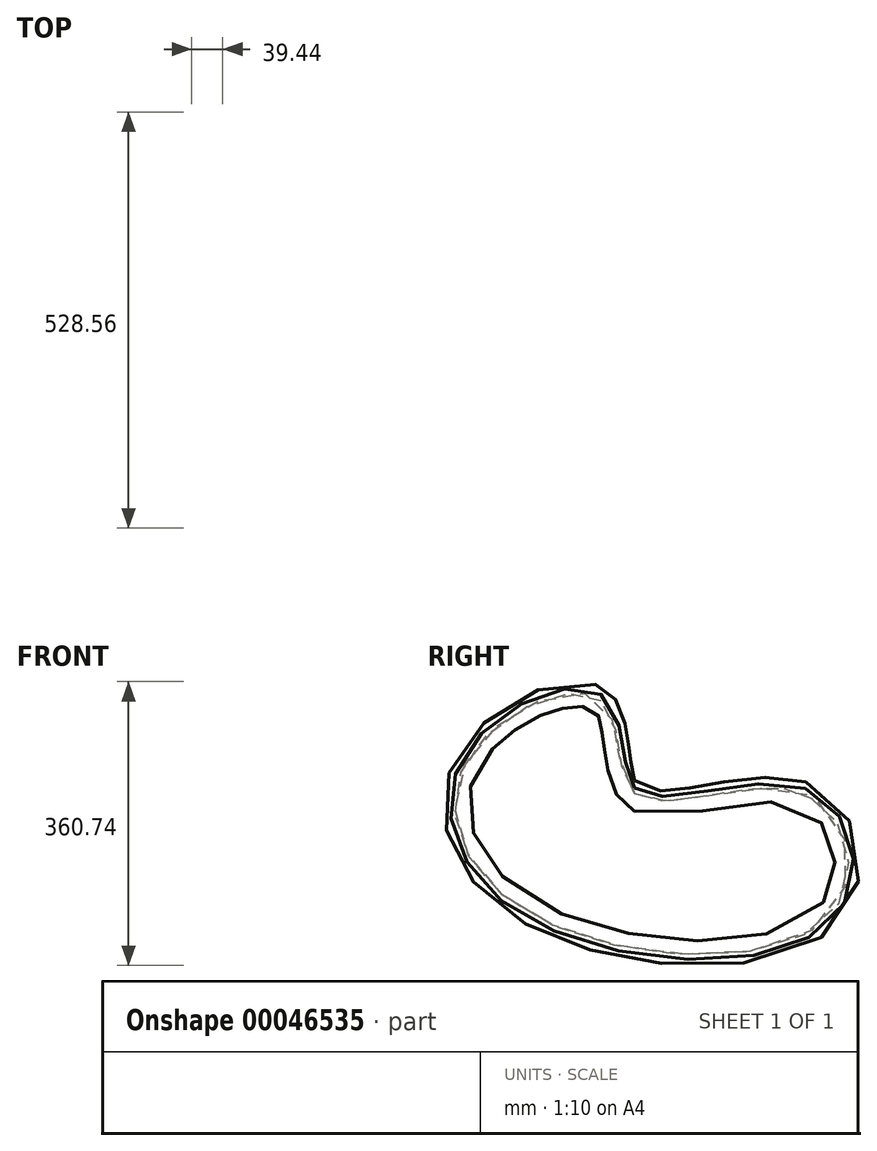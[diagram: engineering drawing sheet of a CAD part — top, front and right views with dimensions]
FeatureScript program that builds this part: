
annotation { "Feature Type Name" : "Feature", "Feature Type Description" : "" }
export const myFeature = defineFeature(function(context is Context, id is Id, definition is map)
    precondition{}
    {
        {
            var Q0;
            Q0=qCreatedBy(makeId("Front.planeOp"),FACE);
            var sketch = newSketch(context, id + "F0", { "sketchPlane" : qUnion([Q0])});
            skCircle(sketch, "E0", {"center": v(0, 0) * mm, "radius": 19.72 * mm});
            skCircle(sketch, "E1", {"center": v(-18.56, 6.66) * mm, "radius": 3.98 * mm});
            skSolve(sketch);
        }
        {
            var Q0;
            Q0=qCreatedBy(makeId("Right.planeOp"),FACE);
            var sketch = newSketch(context, id + "F1", { "sketchPlane" : qUnion([Q0])});
            skFitSpline(sketch, "E2", {"points": [v(0, 0) * mm, v(216.74, 0) * mm, v(247.02, -149.99) * mm, v(-145.22, -140.2) * mm, v(-207.64, 49.86) * mm, v(-44.13, 119.27) * mm, v(0, 0) * mm]});
            skSolve(sketch);
        }
        {
            var Q0;
            {var subQ0=sQuery(id+"F0.wireOp",EDGE,"E1");var subQ1=sQuery(id+"F0.wireOp",EDGE,"E0");var subQ3=makeQuery(id+"F0.imprint","INTERSECT",VERTEX,{"disambiguationData":[OD(0.0)],"derivedFrom":[subQ1,subQ0]});Q0=makeQuery(id+"F0.imprint","IMPRINT",FACE,{"disambiguationData":[TD([[makeQuery(id+"F0.imprint","IMPRINT",EDGE,{"disambiguationData":[TD([[subQ3,-1.0]])],"derivedFrom":subQ1}),1.0]])]});}
            var Q1;
            Q1=sQuery(id+"F1.wireOp",EDGE,"E2");
            sweep(context, id + "F2", {"profiles" : qUnion([Q0]), "path" : qUnion([Q1])});
        }
    });
